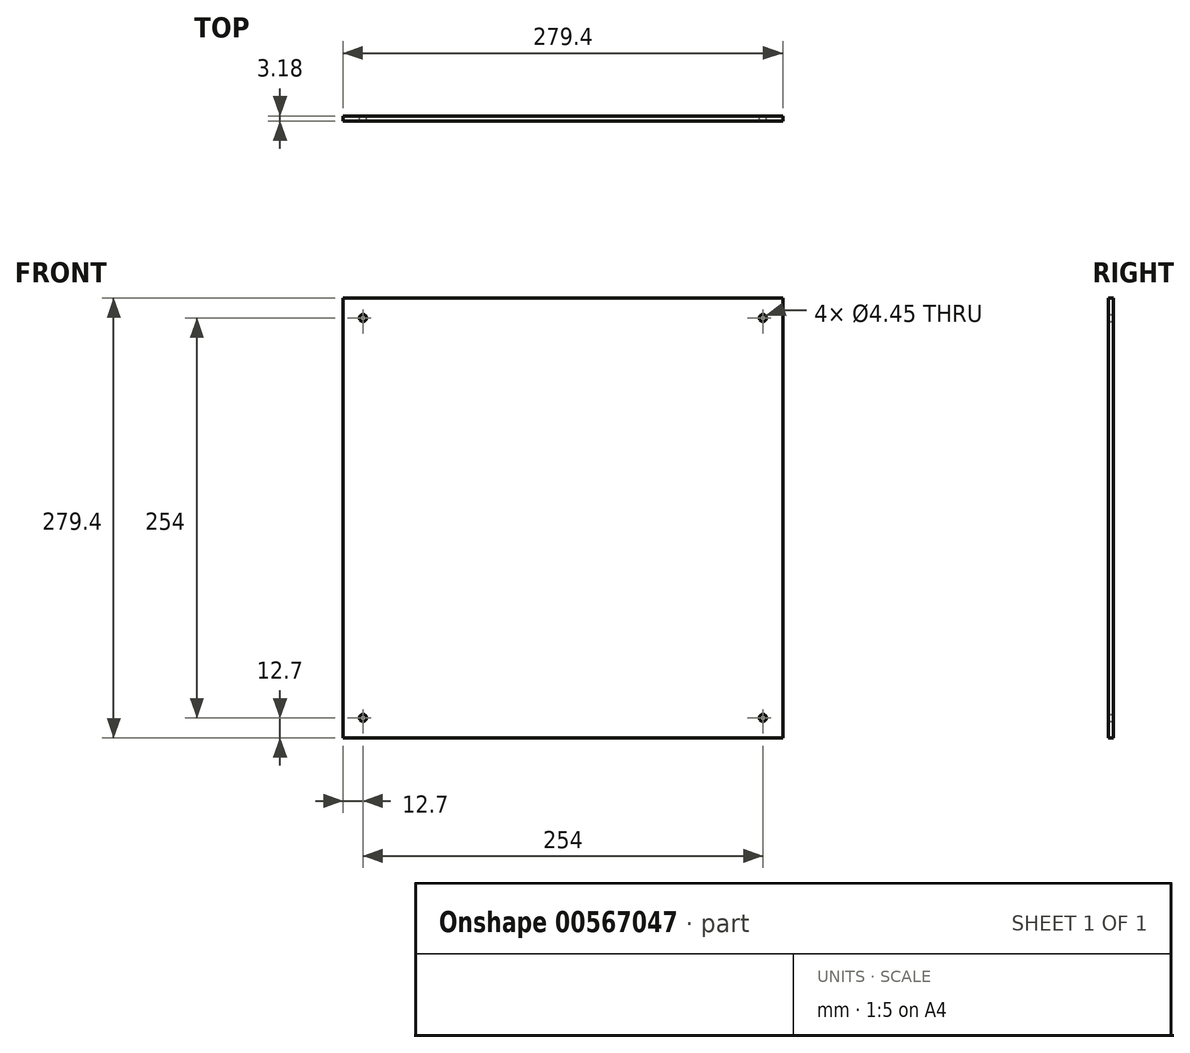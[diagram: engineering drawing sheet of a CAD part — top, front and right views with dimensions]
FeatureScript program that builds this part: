
annotation { "Feature Type Name" : "Feature", "Feature Type Description" : "" }
export const myFeature = defineFeature(function(context is Context, id is Id, definition is map)
    precondition{}
    {
        {
            var Q0;
            Q0=qCreatedBy(makeId("Front.planeOp"),FACE);
            var sketch = newSketch(context, id + "F0", { "sketchPlane" : qUnion([Q0])});
            skLineSegment(sketch, "E0.bottom", {"start": v(-139.7, 139.7) * mm, "end": v(139.7, 139.7) * mm});
            skLineSegment(sketch, "E0.top", {"start": v(-139.7, -139.7) * mm, "end": v(139.7, -139.7) * mm});
            skLineSegment(sketch, "E0.left", {"start": v(-139.7, 139.7) * mm, "end": v(-139.7, -139.7) * mm});
            skLineSegment(sketch, "E0.right", {"start": v(139.7, 139.7) * mm, "end": v(139.7, -139.7) * mm});
            skPoint(sketch, "E0.middle", {"position": v(0, 0) * mm});
            skLineSegment(sketch, "E1.bottom", {"start": v(-127, 127) * mm, "end": v(127, 127) * mm, "construction": true});
            skLineSegment(sketch, "E1.top", {"start": v(-127, -127) * mm, "end": v(127, -127) * mm, "construction": true});
            skLineSegment(sketch, "E1.left", {"start": v(-127, 127) * mm, "end": v(-127, -127) * mm, "construction": true});
            skLineSegment(sketch, "E1.right", {"start": v(127, 127) * mm, "end": v(127, -127) * mm, "construction": true});
            skCircle(sketch, "E2", {"center": v(-127, -127) * mm, "radius": 2.22 * mm});
            skCircle(sketch, "E3", {"center": v(-127, 127) * mm, "radius": 2.22 * mm});
            skCircle(sketch, "E4", {"center": v(127, 127) * mm, "radius": 2.22 * mm});
            skCircle(sketch, "E5", {"center": v(127, -127) * mm, "radius": 2.22 * mm});
            skSolve(sketch);
        }
        {
            var Q0;
            Q0=qSketchRegion(id+"F0",true);
            extrude(context, id + "F1", {"entities" : qUnion([Q0]), "depth" : 3.17 * mm, "offsetDistance" : 25.4 * mm});
        }
    });
